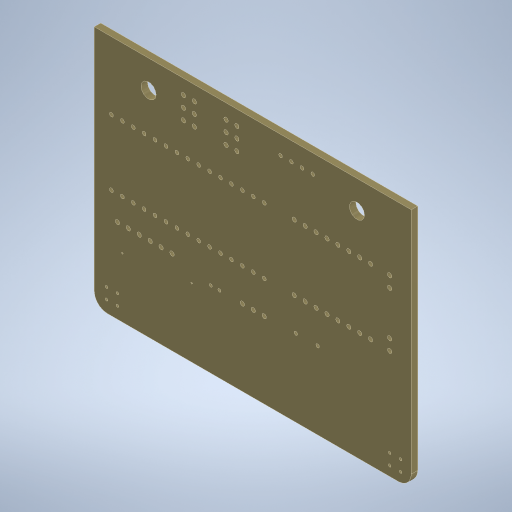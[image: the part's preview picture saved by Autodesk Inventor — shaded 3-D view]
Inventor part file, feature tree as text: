
AUTODESK INVENTOR PART (.ipt)
format: ipt  version: 2023 (Build 270158000, 158)  size: 427,520 bytes
history: native  units: in
note: dims shown in document units (in); Inventor stores cm internally (conversion verified against a paired STEP export)
features: other x2, extrude x1, sketch x1, projected_geometry x1
ambient origin geometry x8: Origin, YZ Plane, XZ Plane, XY Plane, X Axis, Y Axis, Z Axis, Center Point
bodies: Body1 (feature_tree)
feature tree (5):
  other  "Bryła1"
  extrude  "Wyciągnięcie proste2"  TaperAngle=0.0deg  [1 undecoded]
  sketch  "Szkic3"
  projected_geometry  "Pętla rzutowana2"
  other  "Płytka"
note: 1 required parameter value undecoded (feature->parameter linkage not recoverable at this tier; creation-order binding heuristic only, values carry confidence <= 0.55)
